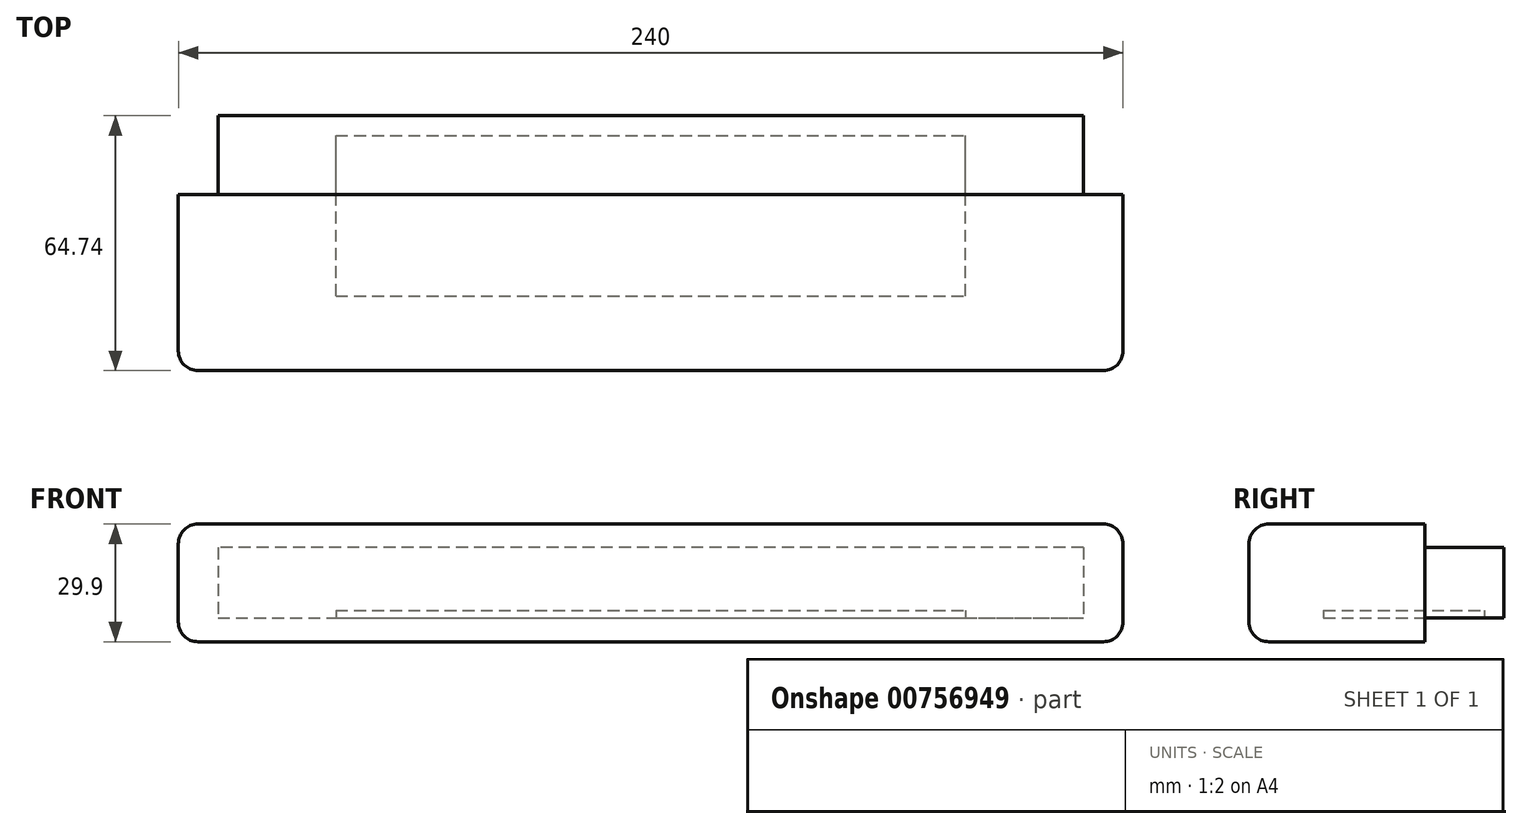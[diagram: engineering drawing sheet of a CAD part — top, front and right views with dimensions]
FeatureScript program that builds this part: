
annotation { "Feature Type Name" : "Feature", "Feature Type Description" : "" }
export const myFeature = defineFeature(function(context is Context, id is Id, definition is map)
    precondition{}
    {
        {
            var Q0;
            Q0=qCreatedBy(makeId("Top.planeOp"),FACE);
            var sketch = newSketch(context, id + "F0", { "sketchPlane" : qUnion([Q0])});
            skLineSegment(sketch, "E0.bottom", {"start": v(-260.45, 64.74) * mm, "end": v(-20.45, 64.74) * mm});
            skLineSegment(sketch, "E0.top", {"start": v(-260.45, 0) * mm, "end": v(-20.45, 0) * mm});
            skLineSegment(sketch, "E0.left", {"start": v(-260.45, 64.74) * mm, "end": v(-260.45, 0) * mm});
            skLineSegment(sketch, "E0.right", {"start": v(-20.45, 64.74) * mm, "end": v(-20.45, 0) * mm});
            skSolve(sketch);
        }
        {
            var Q0;
            Q0=makeQuery(id+"F0.imprint","IMPRINT",FACE,{"disambiguationData":[TD([[makeQuery(id+"F0.imprint","IMPRINT",EDGE,{"derivedFrom":sQuery(id+"F0.wireOp",EDGE,"E0.bottom")}),-1.0]])]});
            extrude(context, id + "F1", {"entities" : qUnion([Q0]), "depth" : 17.9 * mm, "offsetDistance" : 25 * mm});
        }
        {
            var Q0;
            Q0=makeQuery(id+"F1.opExtrude","SWEPT_FACE",FACE,{"disambiguationData":[OSD([sQuery(id+"F0.wireOp",EDGE,"E0.bottom")])]});
            var sketch = newSketch(context, id + "F2", { "sketchPlane" : qUnion([Q0])});
            skLineSegment(sketch, "E1.bottom", {"start": v(20.45, 17.9) * mm, "end": v(30.5, 17.9) * mm});
            skLineSegment(sketch, "E1.top", {"start": v(20.45, 0) * mm, "end": v(30.5, 0) * mm});
            skLineSegment(sketch, "E1.left", {"start": v(20.45, 17.9) * mm, "end": v(20.45, 0) * mm});
            skLineSegment(sketch, "E1.right", {"start": v(30.5, 17.9) * mm, "end": v(30.5, 0) * mm});
            skLineSegment(sketch, "E2.bottom", {"start": v(260.45, 17.9) * mm, "end": v(250.4, 17.9) * mm});
            skLineSegment(sketch, "E2.top", {"start": v(260.45, 0) * mm, "end": v(250.4, 0) * mm});
            skLineSegment(sketch, "E2.left", {"start": v(260.45, 17.9) * mm, "end": v(260.45, 0) * mm});
            skLineSegment(sketch, "E2.right", {"start": v(250.4, 17.9) * mm, "end": v(250.4, 0) * mm});
            skSolve(sketch);
        }
        {
            var Q0;
            Q0=qSketchRegion(id+"F2",true);
            extrude(context, id + "F3", {"entities" : qUnion([Q0]), "operationType" : NewBodyOperationType.REMOVE, "oppositeDirection" : true, "depth" : 20 * mm, "offsetDistance" : 25 * mm});
        }
        {
            var Q0;
            Q0=makeQuery(id+"F1.opExtrude","CAP_FACE",FACE,{"disambiguationData":[OSD([sQuery(id+"F0.wireOp",EDGE,"E0.bottom"),sQuery(id+"F0.wireOp",EDGE,"E0.top"),sQuery(id+"F0.wireOp",EDGE,"E0.left"),sQuery(id+"F0.wireOp",EDGE,"E0.right")])],"isStart":false});
            var sketch = newSketch(context, id + "F4", { "sketchPlane" : qUnion([Q0])});
            skLineSegment(sketch, "E3.bottom", {"start": v(-20.45, 0) * mm, "end": v(-260.45, 0) * mm});
            skLineSegment(sketch, "E3.top", {"start": v(-20.45, 44.74) * mm, "end": v(-260.45, 44.74) * mm});
            skLineSegment(sketch, "E3.left", {"start": v(-20.45, 0) * mm, "end": v(-20.45, 44.74) * mm});
            skLineSegment(sketch, "E3.right", {"start": v(-260.45, 0) * mm, "end": v(-260.45, 44.74) * mm});
            skSolve(sketch);
        }
        {
            var Q0;
            Q0=makeQuery(id+"F1.opExtrude","CAP_FACE",FACE,{"disambiguationData":[OSD([sQuery(id+"F0.wireOp",EDGE,"E0.bottom"),sQuery(id+"F0.wireOp",EDGE,"E0.top"),sQuery(id+"F0.wireOp",EDGE,"E0.left"),sQuery(id+"F0.wireOp",EDGE,"E0.right")])],"isStart":true});
            var sketch = newSketch(context, id + "F5", { "sketchPlane" : qUnion([Q0])});
            skLineSegment(sketch, "E4.bottom", {"start": v(-20.45, -44.74) * mm, "end": v(-260.45, -44.74) * mm});
            skLineSegment(sketch, "E4.top", {"start": v(-20.45, 0) * mm, "end": v(-260.45, 0) * mm});
            skLineSegment(sketch, "E4.left", {"start": v(-20.45, -44.74) * mm, "end": v(-20.45, 0) * mm});
            skLineSegment(sketch, "E4.right", {"start": v(-260.45, -44.74) * mm, "end": v(-260.45, 0) * mm});
            skSolve(sketch);
        }
        {
            var Q0;
            Q0=qSketchRegion(id+"F4",true);
            var Q1;
            Q1=makeQuery(id+"F5.imprint","IMPRINT",FACE,{"disambiguationData":[TD([[makeQuery(id+"F5.imprint","IMPRINT",EDGE,{"derivedFrom":sQuery(id+"F5.wireOp",EDGE,"E4.top")}),-1.0]])]});
            extrude(context, id + "F6", {"entities" : qUnion([Q0, Q1]), "operationType" : NewBodyOperationType.ADD, "depth" : 6 * mm, "offsetDistance" : 25 * mm, "hasSecondDirection" : true, "secondDirectionOppositeDirection" : true, "secondDirectionDepth" : 6 * mm});
        }
        {
            var Q0;
            Q0=makeQuery(id+"F1.opExtrude","CAP_FACE",FACE,{"disambiguationData":[OSD([sQuery(id+"F0.wireOp",EDGE,"E0.bottom"),sQuery(id+"F0.wireOp",EDGE,"E0.top"),sQuery(id+"F0.wireOp",EDGE,"E0.left"),sQuery(id+"F0.wireOp",EDGE,"E0.right")])],"isStart":true});
            var sketch = newSketch(context, id + "F7", { "sketchPlane" : qUnion([Q0])});
            skLineSegment(sketch, "E5.bottom", {"start": v(-220.4, -18.95) * mm, "end": v(-60.5, -18.95) * mm});
            skLineSegment(sketch, "E5.top", {"start": v(-220.4, -59.74) * mm, "end": v(-60.5, -59.74) * mm});
            skLineSegment(sketch, "E5.left", {"start": v(-220.4, -18.95) * mm, "end": v(-220.4, -59.74) * mm});
            skLineSegment(sketch, "E5.right", {"start": v(-60.5, -18.95) * mm, "end": v(-60.5, -59.74) * mm});
            skSolve(sketch);
        }
        {
            var Q0;
            Q0=qSketchRegion(id+"F7",true);
            extrude(context, id + "F8", {"entities" : qUnion([Q0]), "operationType" : NewBodyOperationType.REMOVE, "oppositeDirection" : true, "depth" : 2 * mm, "offsetDistance" : 25 * mm});
        }
        {
            var Q0;
            Q0=makeQuery(id+"F6.opExtrude","CAP_EDGE",EDGE,{"disambiguationData":[OSD([sQuery(id+"F5.wireOp",EDGE,"E4.top")])],"isStart":true});
            var Q1;
            Q1=makeQuery(id+"F6.opExtrude","CAP_EDGE",EDGE,{"disambiguationData":[OSD([sQuery(id+"F4.wireOp",EDGE,"E3.bottom")])],"isStart":false});
            var Q2;
            Q2=makeQuery(id+"F6.boolean.opBoolean","MERGE",EDGE,{"derivedFrom":[makeQuery(id+"F1.opExtrude","SWEPT_EDGE",EDGE,{"disambiguationData":[OSD([sQuery(id+"F0.wireOp",EDGE,"E0.top"),sQuery(id+"F0.wireOp",EDGE,"E0.right")])]}),makeQuery(id+"F6.opExtrude","SWEPT_EDGE",EDGE,{"disambiguationData":[OSD([sQuery(id+"F4.wireOp",EDGE,"E3.bottom"),sQuery(id+"F4.wireOp",EDGE,"E3.left")])]}),makeQuery(id+"F6.opExtrude","SWEPT_EDGE",EDGE,{"disambiguationData":[OSD([sQuery(id+"F5.wireOp",EDGE,"E4.top"),sQuery(id+"F5.wireOp",EDGE,"E4.left")])]})]});
            var Q3;
            Q3=makeQuery(id+"F6.boolean.opBoolean","MERGE",EDGE,{"derivedFrom":[makeQuery(id+"F1.opExtrude","SWEPT_EDGE",EDGE,{"disambiguationData":[OSD([sQuery(id+"F0.wireOp",EDGE,"E0.top"),sQuery(id+"F0.wireOp",EDGE,"E0.left")])]}),makeQuery(id+"F6.opExtrude","SWEPT_EDGE",EDGE,{"disambiguationData":[OSD([sQuery(id+"F4.wireOp",EDGE,"E3.bottom"),sQuery(id+"F4.wireOp",EDGE,"E3.right")])]}),makeQuery(id+"F6.opExtrude","SWEPT_EDGE",EDGE,{"disambiguationData":[OSD([sQuery(id+"F5.wireOp",EDGE,"E4.top"),sQuery(id+"F5.wireOp",EDGE,"E4.right")])]})]});
            var Q4;
            Q4=makeQuery(id+"F6.opExtrude","CAP_EDGE",EDGE,{"disambiguationData":[OSD([sQuery(id+"F5.wireOp",EDGE,"E4.left")])],"isStart":true});
            var Q5;
            Q5=makeQuery(id+"F6.opExtrude","CAP_EDGE",EDGE,{"disambiguationData":[OSD([sQuery(id+"F4.wireOp",EDGE,"E3.left")])],"isStart":false});
            var Q6;
            Q6=makeQuery(id+"F6.opExtrude","CAP_EDGE",EDGE,{"disambiguationData":[OSD([sQuery(id+"F5.wireOp",EDGE,"E4.right")])],"isStart":true});
            var Q7;
            Q7=makeQuery(id+"F6.opExtrude","CAP_EDGE",EDGE,{"disambiguationData":[OSD([sQuery(id+"F4.wireOp",EDGE,"E3.right")])],"isStart":false});
            fillet(context, id + "F9", {"entities" : qUnion([Q0, Q1, Q2, Q3, Q4, Q5, Q6, Q7]), "radius" : 5 * mm, "tangentPropagation" : true, "allowEdgeOverflow" : false});
        }
    });
